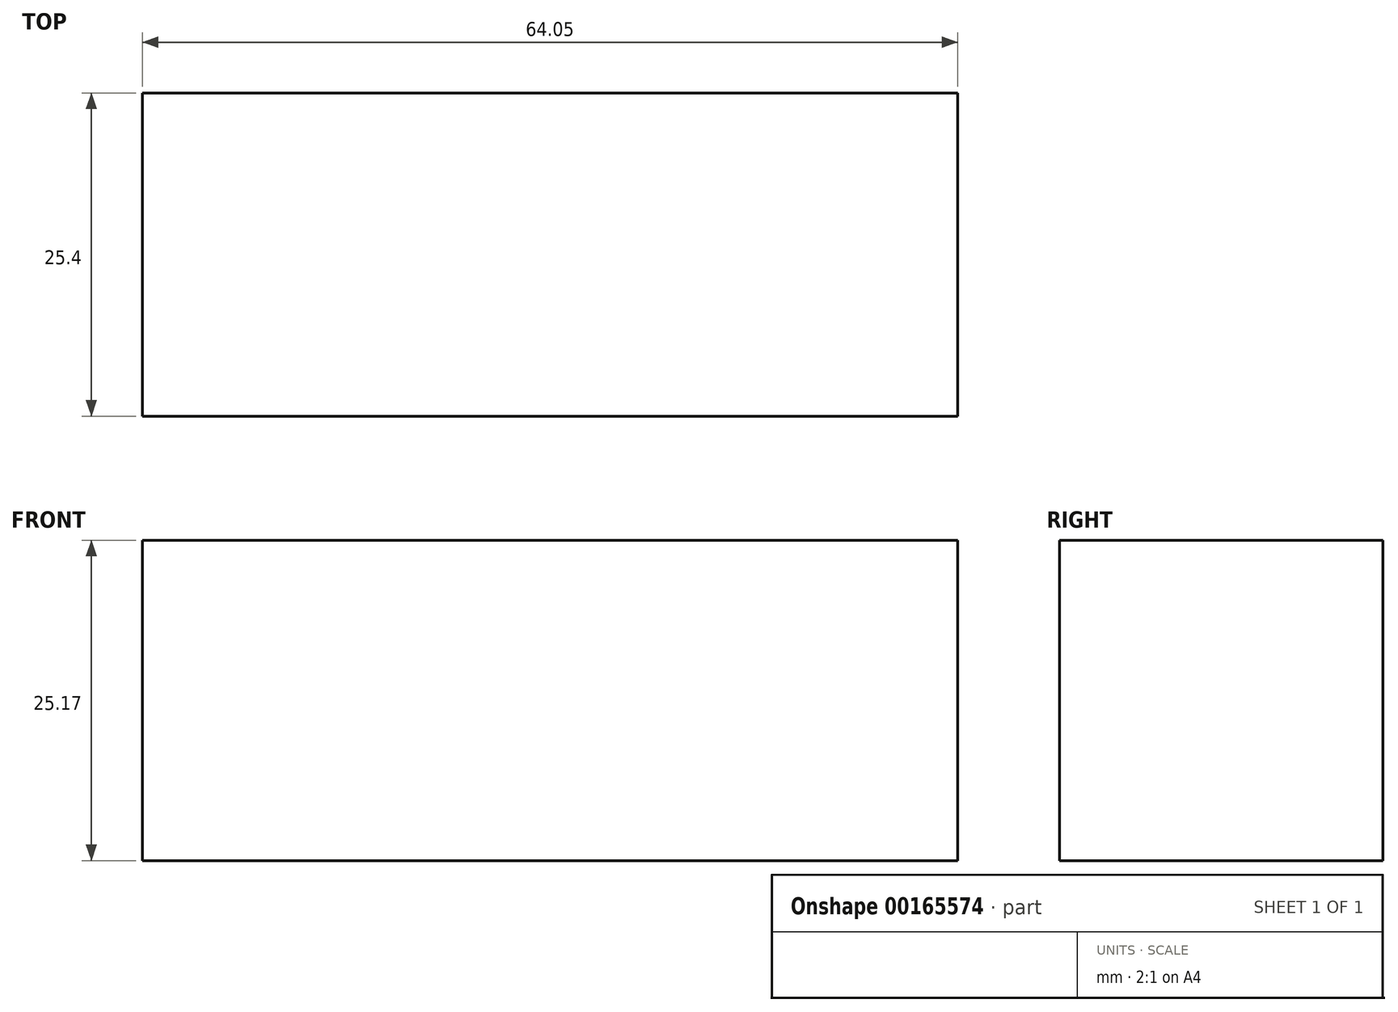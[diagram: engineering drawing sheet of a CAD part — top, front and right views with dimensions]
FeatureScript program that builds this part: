
annotation { "Feature Type Name" : "Feature", "Feature Type Description" : "" }
export const myFeature = defineFeature(function(context is Context, id is Id, definition is map)
    precondition{}
    {
        {
            var Q0;
            Q0=qCreatedBy(makeId("Front.planeOp"),FACE);
            var sketch = newSketch(context, id + "F0", { "sketchPlane" : qUnion([Q0])});
            skLineSegment(sketch, "E0.bottom", {"start": v(0, 0) * mm, "end": v(64.05, 0) * mm});
            skLineSegment(sketch, "E0.top", {"start": v(0, -25.17) * mm, "end": v(64.05, -25.17) * mm});
            skLineSegment(sketch, "E0.left", {"start": v(0, 0) * mm, "end": v(0, -25.17) * mm});
            skLineSegment(sketch, "E0.right", {"start": v(64.05, 0) * mm, "end": v(64.05, -25.17) * mm});
            skSolve(sketch);
        }
        {
            var Q0;
            Q0 = qSketchRegion(id + "F0", true);
            extrude(context, id + "F1", {"entities" : qUnion([Q0]), "depth" : 25.4 * mm});
        }
    });
